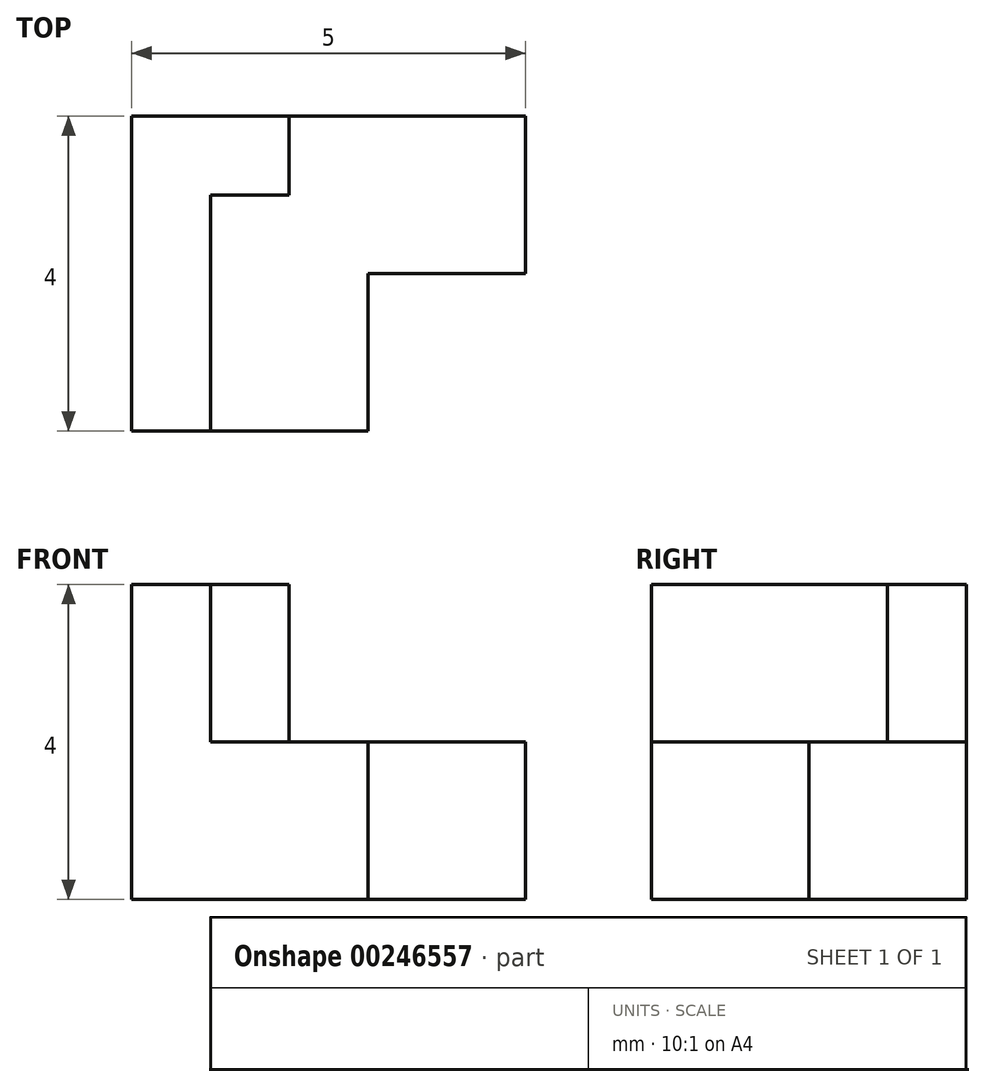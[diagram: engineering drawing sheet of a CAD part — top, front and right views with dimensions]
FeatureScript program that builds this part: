
annotation { "Feature Type Name" : "Feature", "Feature Type Description" : "" }
export const myFeature = defineFeature(function(context is Context, id is Id, definition is map)
    precondition{}
    {
        {
            var Q0;
            Q0=qCreatedBy(makeId("Top.planeOp"),FACE);
            var sketch = newSketch(context, id + "F0", { "sketchPlane" : qUnion([Q0])});
            skLineSegment(sketch, "E0.bottom", {"start": v(0, 4) * mm, "end": v(5, 4) * mm});
            skLineSegment(sketch, "E0.top", {"start": v(0, 0) * mm, "end": v(5, 0) * mm});
            skLineSegment(sketch, "E0.left", {"start": v(0, 4) * mm, "end": v(0, 0) * mm});
            skLineSegment(sketch, "E0.right", {"start": v(5, 4) * mm, "end": v(5, 0) * mm});
            skSolve(sketch);
        }
        {
            var Q0;
            Q0=makeQuery(id+"F0.imprint","IMPRINT",FACE,{"disambiguationData":[TD([[makeQuery(id+"F0.imprint","IMPRINT",EDGE,{"derivedFrom":sQuery(id+"F0.wireOp",EDGE,"E0.bottom")}),-1.0]])]});
            extrude(context, id + "F1", {"entities" : qUnion([Q0]), "depth" : 2 * mm});
        }
        {
            var Q0;
            Q0=makeQuery(id+"F1.opExtrude","CAP_FACE",FACE,{"disambiguationData":[OSD([sQuery(id+"F0.wireOp",EDGE,"E0.bottom"),sQuery(id+"F0.wireOp",EDGE,"E0.top"),sQuery(id+"F0.wireOp",EDGE,"E0.left"),sQuery(id+"F0.wireOp",EDGE,"E0.right")])],"isStart":false});
            var sketch = newSketch(context, id + "F2", { "sketchPlane" : qUnion([Q0])});
            skLineSegment(sketch, "E1.bottom", {"start": v(3, 2) * mm, "end": v(5, 2) * mm});
            skLineSegment(sketch, "E1.top", {"start": v(3, 0) * mm, "end": v(5, 0) * mm});
            skLineSegment(sketch, "E1.left", {"start": v(3, 2) * mm, "end": v(3, 0) * mm});
            skLineSegment(sketch, "E1.right", {"start": v(5, 2) * mm, "end": v(5, 0) * mm});
            skSolve(sketch);
        }
        {
            var Q0;
            Q0=makeQuery(id+"F2.imprint","IMPRINT",FACE,{"disambiguationData":[TD([[makeQuery(id+"F2.imprint","IMPRINT",EDGE,{"derivedFrom":sQuery(id+"F2.wireOp",EDGE,"E1.bottom")}),-1.0]])]});
            extrude(context, id + "F3", {"entities" : qUnion([Q0]), "operationType" : NewBodyOperationType.REMOVE, "oppositeDirection" : true, "depth" : 2 * mm});
        }
        {
            var Q0;
            Q0=makeQuery(id+"F1.opExtrude","CAP_FACE",FACE,{"disambiguationData":[OSD([sQuery(id+"F0.wireOp",EDGE,"E0.bottom"),sQuery(id+"F0.wireOp",EDGE,"E0.top"),sQuery(id+"F0.wireOp",EDGE,"E0.left"),sQuery(id+"F0.wireOp",EDGE,"E0.right")])],"isStart":false});
            var sketch = newSketch(context, id + "F4", { "sketchPlane" : qUnion([Q0])});
            skLineSegment(sketch, "E2.bottom", {"start": v(0, 4) * mm, "end": v(1, 4) * mm});
            skLineSegment(sketch, "E2.top", {"start": v(0, 0) * mm, "end": v(1, 0) * mm});
            skLineSegment(sketch, "E2.left", {"start": v(0, 4) * mm, "end": v(0, 0) * mm});
            skLineSegment(sketch, "E2.right", {"start": v(1, 4) * mm, "end": v(1, 0) * mm});
            skSolve(sketch);
        }
        {
            var Q0;
            Q0=makeQuery(id+"F4.imprint","IMPRINT",FACE,{"disambiguationData":[TD([[makeQuery(id+"F4.imprint","IMPRINT",EDGE,{"derivedFrom":sQuery(id+"F4.wireOp",EDGE,"E2.bottom")}),-1.0]])]});
            extrude(context, id + "F5", {"entities" : qUnion([Q0]), "operationType" : NewBodyOperationType.ADD, "depth" : 2 * mm});
        }
        {
            var Q0;
            Q0=makeQuery(id+"F1.opExtrude","CAP_FACE",FACE,{"disambiguationData":[OSD([sQuery(id+"F0.wireOp",EDGE,"E0.bottom"),sQuery(id+"F0.wireOp",EDGE,"E0.top"),sQuery(id+"F0.wireOp",EDGE,"E0.left"),sQuery(id+"F0.wireOp",EDGE,"E0.right")])],"isStart":false});
            var sketch = newSketch(context, id + "F6", { "sketchPlane" : qUnion([Q0])});
            skLineSegment(sketch, "E3.bottom", {"start": v(1, 4) * mm, "end": v(2, 4) * mm});
            skLineSegment(sketch, "E3.top", {"start": v(1, 3) * mm, "end": v(2, 3) * mm});
            skLineSegment(sketch, "E3.left", {"start": v(1, 4) * mm, "end": v(1, 3) * mm});
            skLineSegment(sketch, "E3.right", {"start": v(2, 4) * mm, "end": v(2, 3) * mm});
            skSolve(sketch);
        }
        {
            var Q0;
            Q0 = qSketchRegion(id + "F6", true);
            extrude(context, id + "F7", {"entities" : qUnion([Q0]), "operationType" : NewBodyOperationType.ADD, "depth" : 2 * mm});
        }
    });
